# Revit family: Sanitary_Urinals_TOTO-USA-Inc_EcoPowerR-Ultra-High-Efficiency-Conceale
name_source: partatom
category: Plumbing Fixtures
revit_build: Autodesk Revit 2015 (Build: 20140606_1530(x64)
units: mm (PartAtom-declared; Revit-internal decimal feet)

## types (1)
- TEU2UA11
    Ambient Temp. = 32°-104°F (0°-40°C)
    BIMobject category = Urinals
    BIMobject category code = sanitary-urinals
    BIMobject main category = Sanitary
    BIMobject main category code = sanitary
    Brand url = https://www.totousa.com
    Description = ECOPOWER® Ultra High-Efficiency Urinal Flush Valve 0.125 GPF
    Discharge Quantity = Preset to 0.125 GPF/ 0.47 LPF
    Edition number = 1
    IFC Classification = Valve
    Installation instructions = https://www.totousa.com
    Manufacturer = TOTO
    Manufacturer name = TOTO USA Inc
    Masterformat 2014 Code = 10 28 00
    Masterformat 2014 Description = Toilet, Bath, and Laundry Accessories
    Material = Metal - TOTO - Stainless Steel
    Material main = Stainless steel
    Model = TEU2UA11
    NBS Reference Code = 35-93-80
    NBS Reference Description = Urinal Flushing Valves
    Nominal height = 0 mm  [stored 0 ft]
    Nominal width = 0 mm  [stored 0 ft]
    OmniClass Code = 23-27 31 00
    OmniClass Description = Valves
    Product Guid = 1d966e45-5823-4413-abd9-727a57d0d44e
    Product SKU = toto-teu2ua11
    Product certification = https://www.totousa.com
    Product data url = https://bimobject.com
    Product family = Toilet and Bath Specialties
    Product group = EcoPower??
    Product url = https://www.totousa.com
    QR code = http://bimobject.com
    Sensor Detection Range = Self-adjusting to environment
    Sensor Detection Time = Factory setting at six (6) seconds minimum
    Technical description = https://www.totousa.com
    UNSPSC Code = 401416
    URL = www.totousa.com
    Uniclass 1.4 Code = L7136
    Uniclass 1.4 Description = Valves
    Uniclass 2015 Code = Pr_40_20_93_79
    Uniclass 2015 Name = Urinal flushing valves
    Warranty = Three year limited
    Water Supply Connection = 19 mm
    Water Supply Pressure(Max) = 861844.6 Pa
    Water Supply Pressure(Min) = 103421.4 Pa

note: [stored X ft] marks values corroborated as IEEE doubles in the binary element streams (Revit-internal decimal feet)

## geometry (parser evidence)
native form markers: Blend x4, Sweep x2
no freeform markers — native parametric forms only
